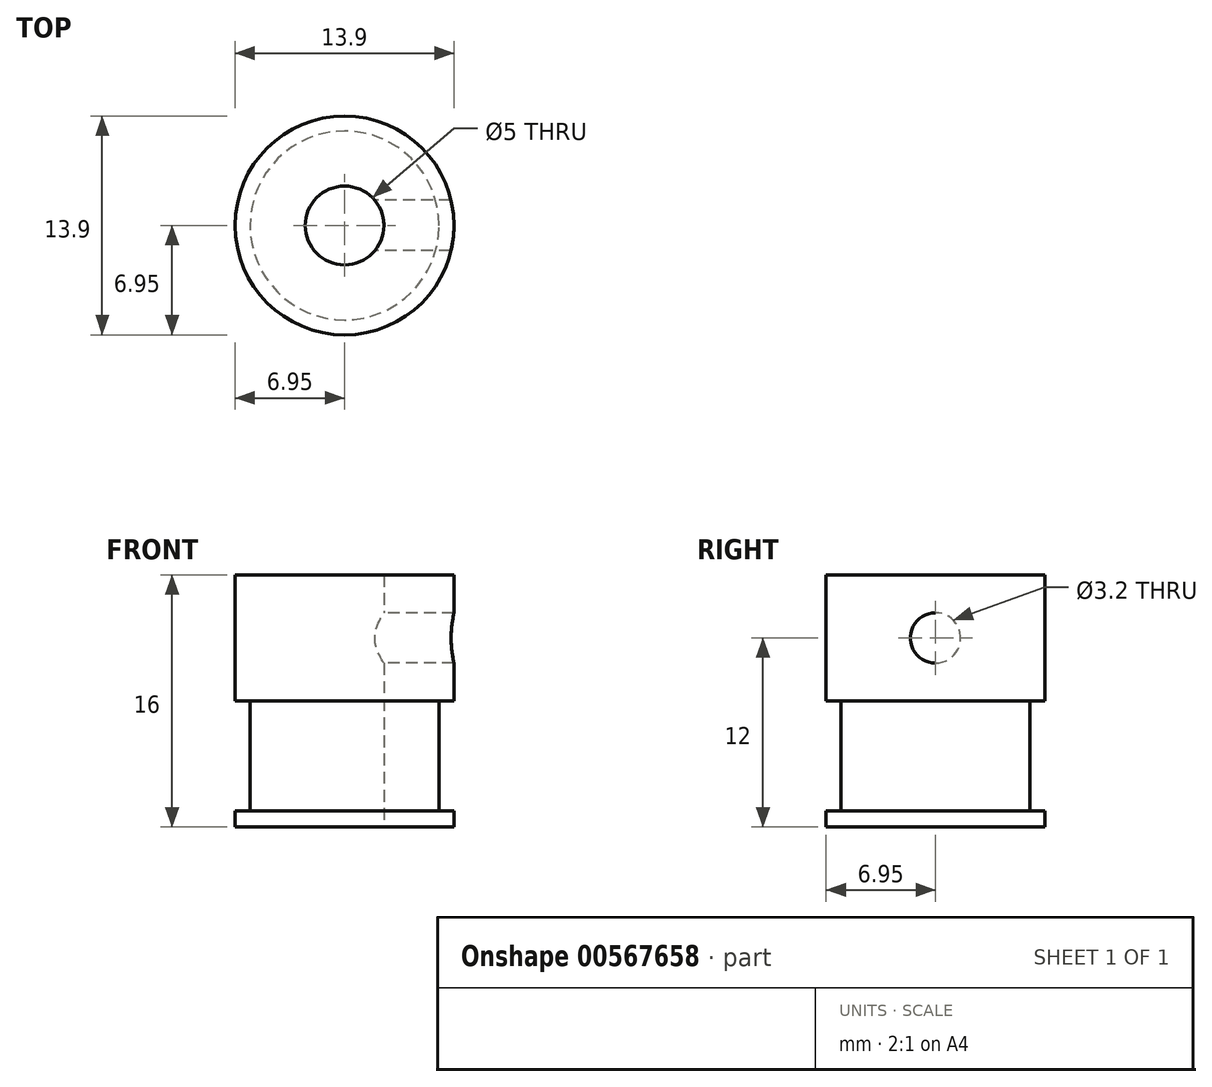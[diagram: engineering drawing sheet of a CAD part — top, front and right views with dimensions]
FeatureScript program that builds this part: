
annotation { "Feature Type Name" : "Feature", "Feature Type Description" : "" }
export const myFeature = defineFeature(function(context is Context, id is Id, definition is map)
    precondition{}
    {
        {
            var Q0;
            Q0=qCreatedBy(makeId("Top.planeOp"),FACE);
            var sketch = newSketch(context, id + "F0", { "sketchPlane" : qUnion([Q0])});
            skCircle(sketch, "E0", {"center": v(0, 0) * mm, "radius": 6.95 * mm});
            skCircle(sketch, "E1", {"center": v(0, 0) * mm, "radius": 6 * mm});
            skCircle(sketch, "E2", {"center": v(0, 0) * mm, "radius": 2.5 * mm});
            skCircle(sketch, "E3", {"center": v(0, 0) * mm, "radius": 4.88 * mm});
            skSolve(sketch);
        }
        {
            var Q0;
            Q0=makeQuery(id+"F0.imprint","IMPRINT",FACE,{"disambiguationData":[TD([[makeQuery(id+"F0.imprint","IMPRINT",EDGE,{"derivedFrom":sQuery(id+"F0.wireOp",EDGE,"E1")}),1.0]])]});
            var Q1;
            Q1=makeQuery(id+"F0.imprint","IMPRINT",FACE,{"disambiguationData":[TD([[makeQuery(id+"F0.imprint","IMPRINT",EDGE,{"derivedFrom":sQuery(id+"F0.wireOp",EDGE,"E0")}),1.0]])]});
            var Q2;
            Q2=makeQuery(id+"F0.imprint","IMPRINT",FACE,{"disambiguationData":[TD([[makeQuery(id+"F0.imprint","IMPRINT",EDGE,{"derivedFrom":sQuery(id+"F0.wireOp",EDGE,"E2")}),-1.0]])]});
            extrude(context, id + "F1", {"entities" : qUnion([Q0, Q1, Q2]), "depth" : 1 * mm, "offsetDistance" : 25 * mm});
        }
        {
            var Q0;
            Q0=makeQuery(id+"F0.imprint","IMPRINT",FACE,{"disambiguationData":[TD([[makeQuery(id+"F0.imprint","IMPRINT",EDGE,{"derivedFrom":sQuery(id+"F0.wireOp",EDGE,"E1")}),1.0]])]});
            var Q1;
            Q1=makeQuery(id+"F0.imprint","IMPRINT",FACE,{"disambiguationData":[TD([[makeQuery(id+"F0.imprint","IMPRINT",EDGE,{"derivedFrom":sQuery(id+"F0.wireOp",EDGE,"E2")}),-1.0]])]});
            extrude(context, id + "F2", {"entities" : qUnion([Q0, Q1]), "operationType" : NewBodyOperationType.ADD, "depth" : 8 * mm, "offsetDistance" : 25 * mm, "hasSecondDirection" : true, "secondDirectionOppositeDirection" : false, "secondDirectionDepth" : 1 * mm});
        }
        {
            var Q0;
            Q0=makeQuery(id+"F0.imprint","IMPRINT",FACE,{"disambiguationData":[TD([[makeQuery(id+"F0.imprint","IMPRINT",EDGE,{"derivedFrom":sQuery(id+"F0.wireOp",EDGE,"E1")}),1.0]])]});
            var Q1;
            Q1=makeQuery(id+"F0.imprint","IMPRINT",FACE,{"disambiguationData":[TD([[makeQuery(id+"F0.imprint","IMPRINT",EDGE,{"derivedFrom":sQuery(id+"F0.wireOp",EDGE,"E0")}),1.0]])]});
            var Q2;
            Q2=makeQuery(id+"F0.imprint","IMPRINT",FACE,{"disambiguationData":[TD([[makeQuery(id+"F0.imprint","IMPRINT",EDGE,{"derivedFrom":sQuery(id+"F0.wireOp",EDGE,"E2")}),-1.0]])]});
            extrude(context, id + "F3", {"entities" : qUnion([Q0, Q1, Q2]), "operationType" : NewBodyOperationType.ADD, "depth" : 9 * mm, "offsetDistance" : 25 * mm, "hasSecondDirection" : true, "secondDirectionOppositeDirection" : false, "secondDirectionDepth" : 8 * mm});
        }
        {
            var Q0;
            Q0=makeQuery(id+"F0.imprint","IMPRINT",FACE,{"disambiguationData":[TD([[makeQuery(id+"F0.imprint","IMPRINT",EDGE,{"derivedFrom":sQuery(id+"F0.wireOp",EDGE,"E2")}),-1.0]])]});
            var Q1;
            Q1=makeQuery(id+"F0.imprint","IMPRINT",FACE,{"disambiguationData":[TD([[makeQuery(id+"F0.imprint","IMPRINT",EDGE,{"derivedFrom":sQuery(id+"F0.wireOp",EDGE,"E0")}),1.0]])]});
            var Q2;
            Q2=makeQuery(id+"F0.imprint","IMPRINT",FACE,{"disambiguationData":[TD([[makeQuery(id+"F0.imprint","IMPRINT",EDGE,{"derivedFrom":sQuery(id+"F0.wireOp",EDGE,"E1")}),1.0]])]});
            extrude(context, id + "F4", {"entities" : qUnion([Q0, Q1, Q2]), "operationType" : NewBodyOperationType.ADD, "depth" : 16 * mm, "offsetDistance" : 25 * mm, "hasSecondDirection" : true, "secondDirectionOppositeDirection" : false, "secondDirectionDepth" : 9 * mm});
        }
        {
            var Q0;
            Q0=qCreatedBy(makeId("Right.planeOp"),FACE);
            var sketch = newSketch(context, id + "F5", { "sketchPlane" : qUnion([Q0])});
            skPoint(sketch, "E4", {"position": v(0, 12) * mm});
            skSolve(sketch);
        }
        {
            var Q0;
            Q0=sQuery(id+"F5.wireOp",VERTEX,"E4");
            var Q1;
            Q1=makeQuery(id+"F1.opExtrude","SWEPT_BODY",BODY,{"disambiguationData":[OSD([sQuery(id+"F0.wireOp",EDGE,"E0"),sQuery(id+"F0.wireOp",EDGE,"E2")])]});
            hole(context, id + "F6", {"style" : HoleStyle.SIMPLE, "endStyle" : HoleEndStyle.THROUGH, "oppositeDirection" : true, "standardTappedOrClearance" : lookupTablePath({ "fit" : "Close", "standard" : "ISO", "size" : "M3", "type" : "Clearance" }), "standardBlindInLast" : lookupTablePath({ "fit" : "Close", "standard" : "ISO", "engagement" : "75%", "pitch" : "0.5 mm", "size" : "M3", "type" : "Clearance & tapped" }), "holeDiameter" : 3.2 * mm, "majorDiameter" : 5 * mm, "isTappedThrough" : true, "tappedDepth" : 12 * mm, "tapClearance" : 3, "locations" : qUnion([Q0]), "scope" : qUnion([Q1])});
        }
    });
